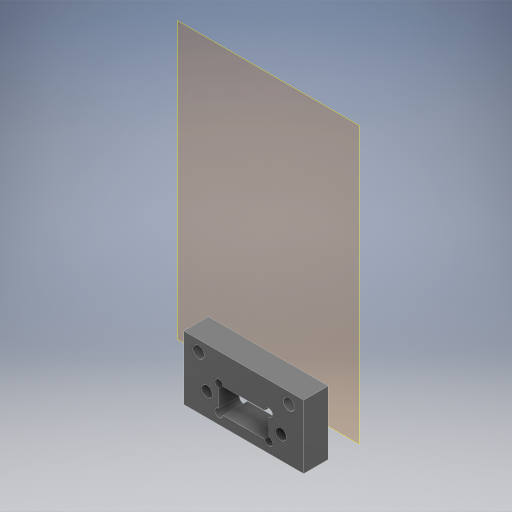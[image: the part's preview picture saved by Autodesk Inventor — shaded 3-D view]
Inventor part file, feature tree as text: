
AUTODESK INVENTOR PART (.ipt)
format: ipt  version: 2024 (Build 280153000, 153)  size: 333,824 bytes
history: native  units: in
note: dims shown in document units (in); Inventor stores cm internally (conversion verified against a paired STEP export)
features: other x4, extrude x2, sketch x2, reference x1
ambient origin geometry x8: Origin, YZ Plane, XZ Plane, XY Plane, X Axis, Y Axis, Z Axis, Center Point
bodies: Body1 (feature_tree)
feature tree (9):
  other  "작업 평면1"
  extrude  "돌출2"  Depth=0.0039in
  extrude  "돌출3"  Depth=0.3543in
  sketch  "스케치1"
  reference  "참조1"
  sketch  "스케치2"
  other  "조립품3"
  other  "MX-64T+idle.ipt:1"
  other  "MX-64T:1"
